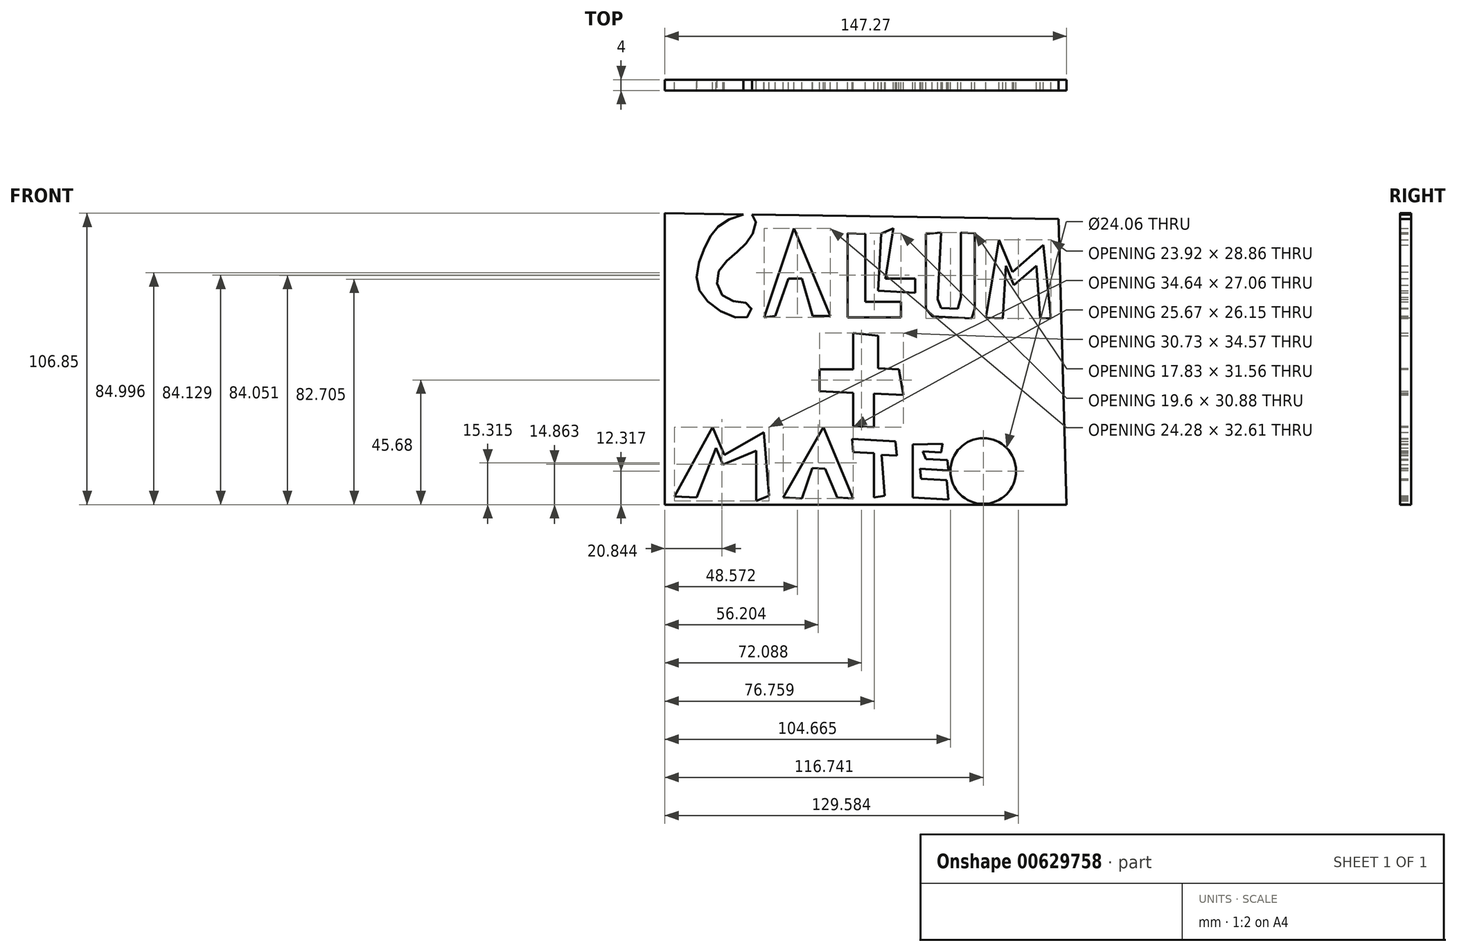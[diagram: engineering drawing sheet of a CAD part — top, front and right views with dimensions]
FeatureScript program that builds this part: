
annotation { "Feature Type Name" : "Feature", "Feature Type Description" : "" }
export const myFeature = defineFeature(function(context is Context, id is Id, definition is map)
    precondition{}
    {
        {
            var Q0;
            Q0=qCreatedBy(makeId("Front.planeOp"),FACE);
            var sketch = newSketch(context, id + "F0", { "sketchPlane" : qUnion([Q0])});
            skFitSpline(sketch, "E0", {"points": [v(-51.52, 49.87) * mm, v(-57.76, 42.93) * mm, v(-61.92, 29.05) * mm, v(-55.68, 18.82) * mm, v(-43.36, 15) * mm, v(-42.32, 19.34) * mm, v(-50.82, 21.6) * mm, v(-54.3, 30.27) * mm, v(-47.35, 38.6) * mm, v(-41.1, 45.88) * mm, v(-41.1, 52.3) * mm, v(-51.52, 49.87) * mm]});
            skLineSegment(sketch, "E1", {"start": v(-37.12, 14.83) * mm, "end": v(-26.2, 47.44) * mm});
            skLineSegment(sketch, "E2", {"start": v(-26.2, 47.44) * mm, "end": v(-12.84, 15.35) * mm});
            skLineSegment(sketch, "E3", {"start": v(-12.84, 15.35) * mm, "end": v(-19.43, 15.35) * mm});
            skLineSegment(sketch, "E4", {"start": v(-19.43, 15.35) * mm, "end": v(-23.24, 29.05) * mm});
            skLineSegment(sketch, "E5", {"start": v(-23.24, 29.05) * mm, "end": v(-28.27, 29.05) * mm});
            skLineSegment(sketch, "E6", {"start": v(-28.27, 29.05) * mm, "end": v(-33.13, 15.35) * mm});
            skLineSegment(sketch, "E7", {"start": v(-33.13, 15.35) * mm, "end": v(-37.12, 14.83) * mm});
            skLineSegment(sketch, "E8", {"start": v(-28.27, 31.4) * mm, "end": v(-23.24, 31.4) * mm});
            skPoint(sketch, "E8.startSnap0", {"position": v(-19.51, 31.4) * mm});
            skLineSegment(sketch, "E9", {"start": v(-23.24, 31.4) * mm, "end": v(-26.2, 38.48) * mm});
            skLineSegment(sketch, "E10", {"start": v(-26.2, 38.48) * mm, "end": v(-28.27, 31.4) * mm});
            skLineSegment(sketch, "E11", {"start": v(-6.6, 45.7) * mm, "end": v(-6.6, 14.83) * mm});
            skLineSegment(sketch, "E12", {"start": v(-6.6, 14.83) * mm, "end": v(13, 14.83) * mm});
            skLineSegment(sketch, "E13", {"start": v(13, 14.83) * mm, "end": v(13, 20.55) * mm});
            skLineSegment(sketch, "E14", {"start": v(13, 20.55) * mm, "end": v(0, 20.55) * mm});
            skLineSegment(sketch, "E15", {"start": v(0, 20.55) * mm, "end": v(0, 45.36) * mm});
            skLineSegment(sketch, "E16", {"start": v(0, 45.36) * mm, "end": v(-6.6, 45.7) * mm});
            skLineSegment(sketch, "E17", {"start": v(5.72, 45.53) * mm, "end": v(4.62, 24.54) * mm});
            skPoint(sketch, "E17.startSnap0", {"position": v(-3.3, 45.53) * mm});
            skLineSegment(sketch, "E18", {"start": v(4.62, 24.54) * mm, "end": v(18.21, 23.82) * mm});
            skLineSegment(sketch, "E19", {"start": v(18.21, 23.82) * mm, "end": v(18.21, 29.05) * mm});
            skLineSegment(sketch, "E20", {"start": v(18.21, 29.05) * mm, "end": v(7.29, 29.05) * mm});
            skLineSegment(sketch, "E21", {"start": v(7.29, 29.05) * mm, "end": v(10.23, 47.44) * mm});
            skLineSegment(sketch, "E22", {"start": v(10.23, 47.44) * mm, "end": v(5.72, 45.53) * mm});
            skLineSegment(sketch, "E23", {"start": v(22.2, 45.36) * mm, "end": v(22.2, 17.95) * mm});
            skLineSegment(sketch, "E24", {"start": v(22.2, 17.95) * mm, "end": v(24.46, 15.18) * mm});
            skLineSegment(sketch, "E25", {"start": v(24.46, 15.18) * mm, "end": v(27.1, 15.04) * mm});
            skLineSegment(sketch, "E26", {"start": v(27.1, 15.04) * mm, "end": v(30.38, 14.87) * mm});
            skLineSegment(sketch, "E27", {"start": v(30.38, 14.87) * mm, "end": v(35.02, 14.62) * mm});
            skLineSegment(sketch, "E28", {"start": v(35.02, 14.62) * mm, "end": v(38.99, 14.41) * mm});
            skLineSegment(sketch, "E29", {"start": v(38.99, 14.41) * mm, "end": v(40.03, 17.95) * mm});
            skLineSegment(sketch, "E30", {"start": v(40.03, 17.95) * mm, "end": v(40.03, 24.54) * mm});
            skLineSegment(sketch, "E31", {"start": v(40.03, 24.54) * mm, "end": v(40.03, 33.74) * mm});
            skLineSegment(sketch, "E32", {"start": v(40.03, 33.74) * mm, "end": v(40.03, 45.7) * mm});
            skLineSegment(sketch, "E33", {"start": v(40.03, 45.7) * mm, "end": v(35.02, 45.97) * mm});
            skLineSegment(sketch, "E34", {"start": v(35.02, 45.97) * mm, "end": v(35.02, 22.12) * mm});
            skLineSegment(sketch, "E35", {"start": v(35.02, 22.12) * mm, "end": v(33.8, 17.95) * mm});
            skLineSegment(sketch, "E36", {"start": v(33.8, 17.95) * mm, "end": v(27.74, 18.27) * mm});
            skLineSegment(sketch, "E37", {"start": v(27.74, 18.27) * mm, "end": v(26.45, 21.37) * mm});
            skLineSegment(sketch, "E38", {"start": v(26.45, 21.37) * mm, "end": v(27.75, 45.97) * mm});
            skLineSegment(sketch, "E39", {"start": v(27.75, 45.97) * mm, "end": v(22.2, 45.36) * mm});
            skLineSegment(sketch, "E40", {"start": v(50.3, 14.41) * mm, "end": v(44.07, 14.74) * mm});
            skLineSegment(sketch, "E41", {"start": v(44.07, 14.74) * mm, "end": v(48.92, 43.28) * mm});
            skLineSegment(sketch, "E42", {"start": v(48.92, 43.28) * mm, "end": v(53.86, 31.4) * mm});
            skLineSegment(sketch, "E43", {"start": v(53.86, 31.4) * mm, "end": v(65.22, 41.37) * mm});
            skLineSegment(sketch, "E44", {"start": v(65.22, 41.37) * mm, "end": v(68, 14.41) * mm});
            skLineSegment(sketch, "E45", {"start": v(68, 14.41) * mm, "end": v(64.03, 14.62) * mm});
            skLineSegment(sketch, "E46", {"start": v(64.03, 14.62) * mm, "end": v(62.62, 33.74) * mm});
            skLineSegment(sketch, "E47", {"start": v(62.62, 33.74) * mm, "end": v(54.47, 26.63) * mm});
            skLineSegment(sketch, "E48", {"start": v(54.47, 26.63) * mm, "end": v(51.5, 33.74) * mm});
            skLineSegment(sketch, "E49", {"start": v(51.5, 33.74) * mm, "end": v(50.3, 14.41) * mm});
            skLineSegment(sketch, "E50", {"start": v(-4.5, 9.1) * mm, "end": v(-4.5, -4.25) * mm});
            skLineSegment(sketch, "E51", {"start": v(-4.5, -4.25) * mm, "end": v(-16.83, -4.25) * mm});
            skLineSegment(sketch, "E52", {"start": v(-16.83, -4.25) * mm, "end": v(-16.83, -12.23) * mm});
            skLineSegment(sketch, "E53", {"start": v(-16.83, -12.23) * mm, "end": v(-4.5, -12.88) * mm});
            skLineSegment(sketch, "E54", {"start": v(-4.5, -12.88) * mm, "end": v(-4.5, -25.06) * mm});
            skLineSegment(sketch, "E55", {"start": v(-4.5, -25.06) * mm, "end": v(3.14, -25.47) * mm});
            skLineSegment(sketch, "E56", {"start": v(3.14, -25.47) * mm, "end": v(3.14, -13.1) * mm});
            skLineSegment(sketch, "E57", {"start": v(3.14, -13.1) * mm, "end": v(13.9, -13.66) * mm});
            skLineSegment(sketch, "E58", {"start": v(13.9, -13.66) * mm, "end": v(12.32, -4.25) * mm});
            skLineSegment(sketch, "E59", {"start": v(12.32, -4.25) * mm, "end": v(4.62, -3.84) * mm});
            skLineSegment(sketch, "E60", {"start": v(4.62, -3.84) * mm, "end": v(4.62, 8.07) * mm});
            skLineSegment(sketch, "E61", {"start": v(4.62, 8.07) * mm, "end": v(-4.5, 9.1) * mm});
            skLineSegment(sketch, "E62", {"start": v(-61.92, -51.26) * mm, "end": v(-70.03, -50.83) * mm});
            skLineSegment(sketch, "E63", {"start": v(-70.03, -50.83) * mm, "end": v(-56.03, -25.47) * mm});
            skLineSegment(sketch, "E64", {"start": v(-56.03, -25.47) * mm, "end": v(-51.8, -35.6) * mm});
            skLineSegment(sketch, "E65", {"start": v(-51.8, -35.6) * mm, "end": v(-37.3, -27.32) * mm});
            skLineSegment(sketch, "E66", {"start": v(-37.3, -27.32) * mm, "end": v(-35.39, -50.56) * mm});
            skLineSegment(sketch, "E67", {"start": v(-35.39, -50.56) * mm, "end": v(-40.1, -52.53) * mm});
            skLineSegment(sketch, "E68", {"start": v(-40.1, -52.53) * mm, "end": v(-40.1, -34.08) * mm});
            skLineSegment(sketch, "E69", {"start": v(-40.1, -34.08) * mm, "end": v(-52.23, -39.13) * mm});
            skLineSegment(sketch, "E70", {"start": v(-52.23, -39.13) * mm, "end": v(-54.74, -33.1) * mm});
            skLineSegment(sketch, "E71", {"start": v(-54.74, -33.1) * mm, "end": v(-61.92, -51.26) * mm});
            skLineSegment(sketch, "E72", {"start": v(-30.18, -51.26) * mm, "end": v(-23.24, -51.62) * mm});
            skLineSegment(sketch, "E73", {"start": v(-23.24, -51.62) * mm, "end": v(-19.51, -40.5) * mm});
            skLineSegment(sketch, "E74", {"start": v(-19.51, -40.5) * mm, "end": v(-14.77, -40.74) * mm});
            skLineSegment(sketch, "E75", {"start": v(-14.77, -40.74) * mm, "end": v(-10.39, -51.26) * mm});
            skLineSegment(sketch, "E76", {"start": v(-10.39, -51.26) * mm, "end": v(-4.5, -51.57) * mm});
            skLineSegment(sketch, "E77", {"start": v(-4.5, -51.57) * mm, "end": v(-15.37, -25.47) * mm});
            skLineSegment(sketch, "E78", {"start": v(-15.37, -25.47) * mm, "end": v(-30.18, -51.26) * mm});
            skLineSegment(sketch, "E79", {"start": v(-19.51, -37.55) * mm, "end": v(-14.77, -37.8) * mm});
            skLineSegment(sketch, "E80", {"start": v(-14.77, -37.8) * mm, "end": v(-16.64, -33.3) * mm});
            skLineSegment(sketch, "E81", {"start": v(-16.64, -33.3) * mm, "end": v(-19.51, -37.55) * mm});
            skLineSegment(sketch, "E82", {"start": v(3.14, -51.26) * mm, "end": v(3.14, -34.95) * mm});
            skLineSegment(sketch, "E83", {"start": v(3.14, -34.95) * mm, "end": v(-4.5, -34.55) * mm});
            skLineSegment(sketch, "E84", {"start": v(-4.5, -34.55) * mm, "end": v(-4.9, -29.78) * mm});
            skLineSegment(sketch, "E85", {"start": v(-4.9, -29.78) * mm, "end": v(11.04, -30.62) * mm});
            skLineSegment(sketch, "E86", {"start": v(11.04, -30.62) * mm, "end": v(11.47, -35.92) * mm});
            skLineSegment(sketch, "E87", {"start": v(11.47, -35.92) * mm, "end": v(5.86, -35.62) * mm});
            skLineSegment(sketch, "E88", {"start": v(5.86, -35.62) * mm, "end": v(7.09, -50.56) * mm});
            skLineSegment(sketch, "E89", {"start": v(7.09, -50.56) * mm, "end": v(3.14, -51.26) * mm});
            skLineSegment(sketch, "E90", {"start": v(17.35, -31.83) * mm, "end": v(17.35, -51.26) * mm});
            skLineSegment(sketch, "E91", {"start": v(17.35, -51.26) * mm, "end": v(30.38, -51.94) * mm});
            skLineSegment(sketch, "E92", {"start": v(30.38, -51.94) * mm, "end": v(29.8, -44.84) * mm});
            skLineSegment(sketch, "E93", {"start": v(29.8, -44.84) * mm, "end": v(20.34, -44.34) * mm});
            skLineSegment(sketch, "E94", {"start": v(20.34, -44.34) * mm, "end": v(20.04, -40.74) * mm});
            skLineSegment(sketch, "E95", {"start": v(20.04, -40.74) * mm, "end": v(30.38, -41.29) * mm});
            skLineSegment(sketch, "E96", {"start": v(30.38, -41.29) * mm, "end": v(30.07, -37.55) * mm});
            skLineSegment(sketch, "E97", {"start": v(30.07, -37.55) * mm, "end": v(22.2, -37.14) * mm});
            skLineSegment(sketch, "E98", {"start": v(22.2, -37.14) * mm, "end": v(21.04, -34.35) * mm});
            skLineSegment(sketch, "E99", {"start": v(21.04, -34.35) * mm, "end": v(27.74, -34.7) * mm});
            skLineSegment(sketch, "E100", {"start": v(27.74, -34.7) * mm, "end": v(28.28, -31.51) * mm});
            skLineSegment(sketch, "E101", {"start": v(28.28, -31.51) * mm, "end": v(17.35, -31.83) * mm});
            skCircle(sketch, "E102", {"center": v(43.2, -41.54) * mm, "radius": 12.03 * mm});
            skLineSegment(sketch, "E103", {"start": v(-73.55, 53) * mm, "end": v(-73.55, -53.86) * mm});
            skLineSegment(sketch, "E104", {"start": v(-73.55, -53.86) * mm, "end": v(73.72, -53.86) * mm});
            skLineSegment(sketch, "E105", {"start": v(73.72, -53.86) * mm, "end": v(70.77, 50.9) * mm});
            skLineSegment(sketch, "E106", {"start": v(70.77, 50.9) * mm, "end": v(-73.55, 53) * mm});
            skSolve(sketch);
        }
        {
            var Q0;
            Q0=makeQuery(id+"F0.imprint","IMPRINT",FACE,{"disambiguationData":[TD([[makeQuery(id+"F0.imprint","IMPRINT",EDGE,{"derivedFrom":sQuery(id+"F0.wireOp",EDGE,"E1")}),1.0]])]});
            extrude(context, id + "F1", {"entities" : qUnion([Q0]), "depth" : 4 * mm, "offsetDistance" : 25 * mm});
        }
    });
